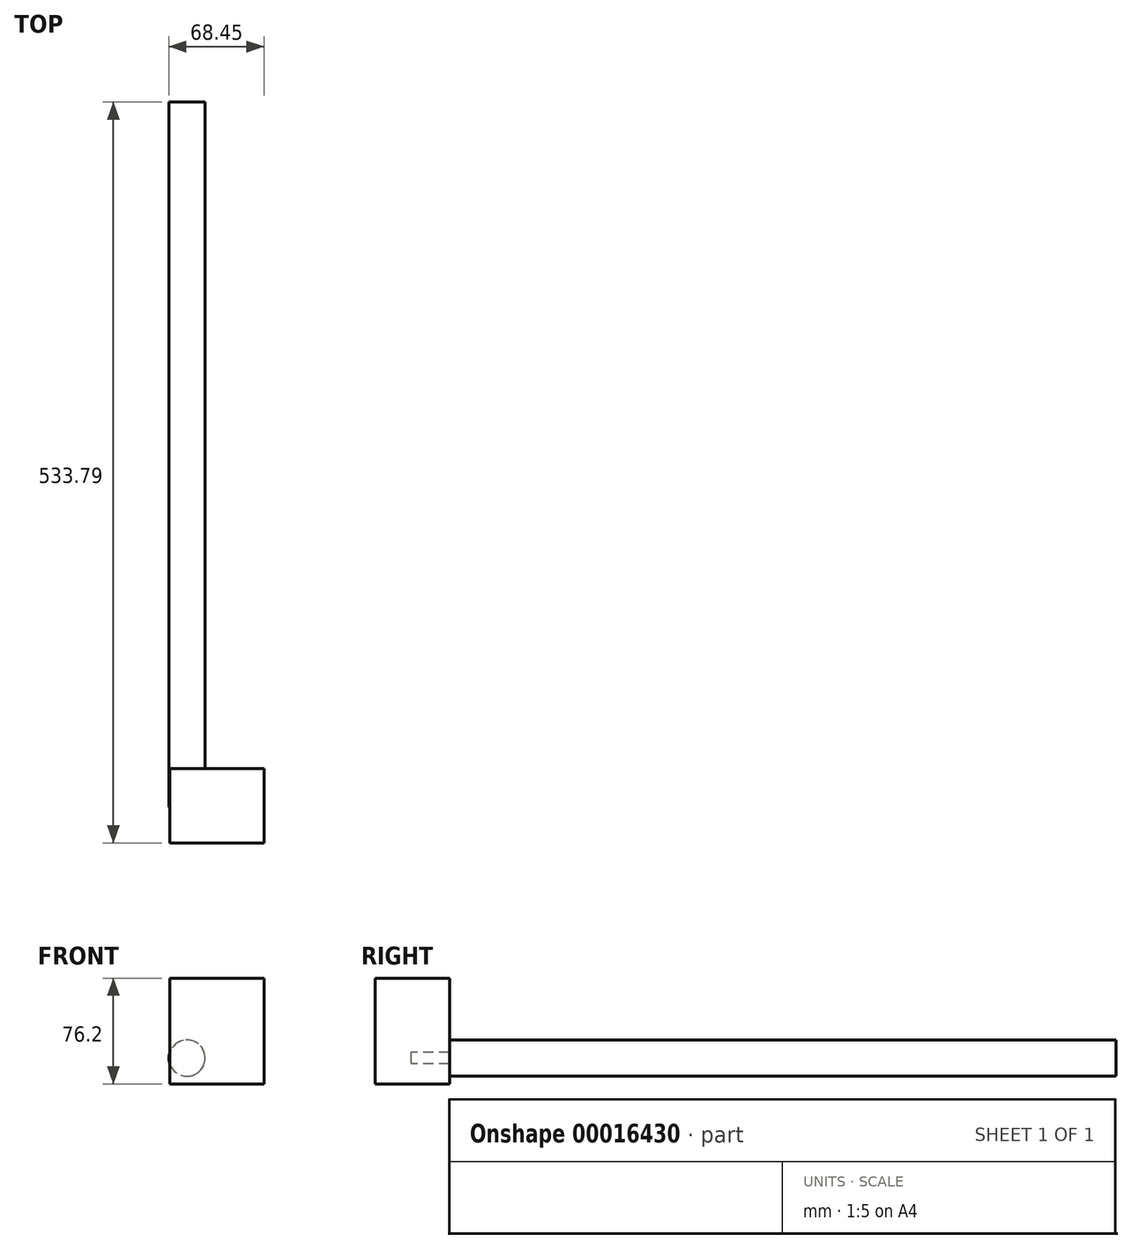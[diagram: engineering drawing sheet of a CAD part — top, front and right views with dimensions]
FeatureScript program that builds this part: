
annotation { "Feature Type Name" : "Feature", "Feature Type Description" : "" }
export const myFeature = defineFeature(function(context is Context, id is Id, definition is map)
    precondition{}
    {
        {
            var Q0;
            Q0=qCreatedBy(makeId("Top.planeOp"),FACE);
            var sketch = newSketch(context, id + "F0", { "sketchPlane" : qUnion([Q0])});
            skLineSegment(sketch, "E0.bottom", {"start": v(-35.8, 27.84) * mm, "end": v(31.95, 27.84) * mm});
            skLineSegment(sketch, "E0.top", {"start": v(-35.8, -25.8) * mm, "end": v(31.95, -25.8) * mm});
            skLineSegment(sketch, "E0.left", {"start": v(-35.8, 27.84) * mm, "end": v(-35.8, -25.8) * mm});
            skLineSegment(sketch, "E0.right", {"start": v(31.95, 27.84) * mm, "end": v(31.95, -25.8) * mm});
            skSolve(sketch);
        }
        {
            var Q0;
            Q0 = qSketchRegion(id + "F0", true);
            extrude(context, id + "F1", {"entities" : qUnion([Q0]), "depth" : 76.2 * mm});
        }
        {
            var Q0;
            Q0=qCreatedBy(makeId("Front.planeOp"),FACE);
            var sketch = newSketch(context, id + "F2", { "sketchPlane" : qUnion([Q0])});
            skCircle(sketch, "E1", {"center": v(-23.45, 18.55) * mm, "radius": 13.04 * mm});
            skSolve(sketch);
        }
        {
            var Q0;
            Q0 = qSketchRegion(id + "F2", true);
            extrude(context, id + "F3", {"entities" : qUnion([Q0]), "operationType" : NewBodyOperationType.ADD, "oppositeDirection" : true, "depth" : 508 * mm});
        }
    });
